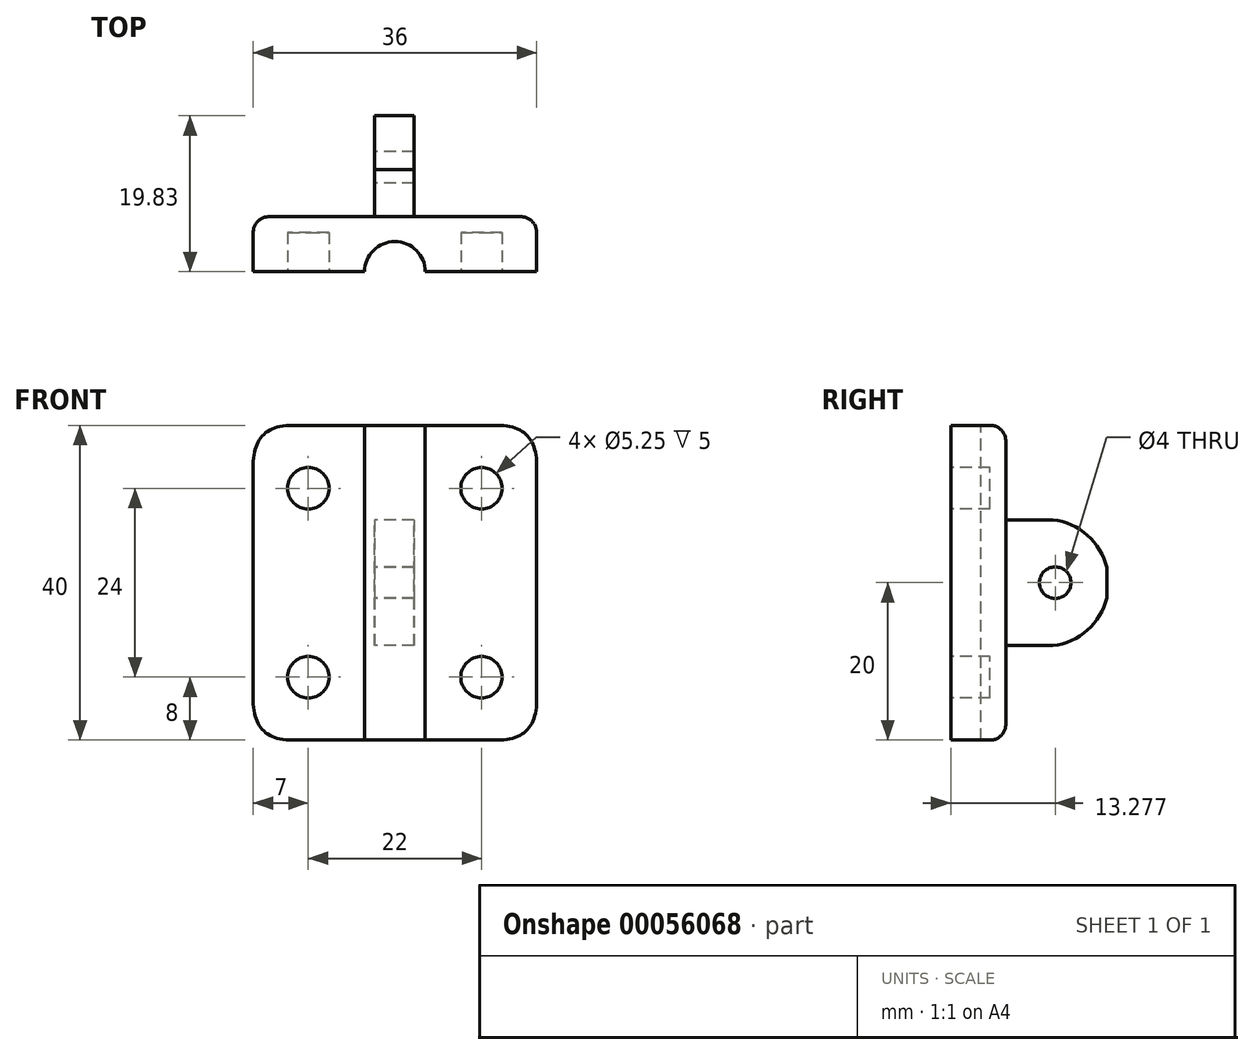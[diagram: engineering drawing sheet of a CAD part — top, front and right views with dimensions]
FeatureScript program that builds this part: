
annotation { "Feature Type Name" : "Feature", "Feature Type Description" : "" }
export const myFeature = defineFeature(function(context is Context, id is Id, definition is map)
    precondition{}
    {
        {
            var Q0;
            Q0=qCreatedBy(makeId("Top.planeOp"),FACE);
            var sketch = newSketch(context, id + "F0", { "sketchPlane" : qUnion([Q0])});
            skLineSegment(sketch, "E0.bottom", {"start": v(-18, 0) * mm, "end": v(18, 0) * mm});
            skLineSegment(sketch, "E0.top", {"start": v(-18, 7) * mm, "end": v(18, 7) * mm});
            skLineSegment(sketch, "E0.left", {"start": v(-18, 0) * mm, "end": v(-18, 7) * mm});
            skLineSegment(sketch, "E0.right", {"start": v(18, 0) * mm, "end": v(18, 7) * mm});
            skSolve(sketch);
        }
        {
            var Q0;
            Q0=makeQuery(id+"F0.imprint","IMPRINT",FACE,{"disambiguationData":[TD([[makeQuery(id+"F0.imprint","IMPRINT",EDGE,{"derivedFrom":sQuery(id+"F0.wireOp",EDGE,"E0.bottom")}),1.0]])]});
            extrude(context, id + "F1", {"entities" : qUnion([Q0]), "depth" : 40 * mm});
        }
        {
            var Q0;
            Q0=makeQuery(id+"F1.opExtrude","CAP_FACE",FACE,{"disambiguationData":[OSD([sQuery(id+"F0.wireOp",EDGE,"E0.bottom"),sQuery(id+"F0.wireOp",EDGE,"E0.top"),sQuery(id+"F0.wireOp",EDGE,"E0.left"),sQuery(id+"F0.wireOp",EDGE,"E0.right")])],"isStart":false});
            var sketch = newSketch(context, id + "F2", { "sketchPlane" : qUnion([Q0])});
            skCircle(sketch, "E1", {"center": v(0, 0) * mm, "radius": 3.85 * mm});
            skSolve(sketch);
        }
        {
            var Q0;
            {var subQ0=sQuery(id+"F2.wireOp",EDGE,"E1");var subQ1=makeQuery(id+"F1.opExtrude","CAP_EDGE",EDGE,{"disambiguationData":[OSD([sQuery(id+"F0.wireOp",EDGE,"E0.bottom")])],"isStart":false});var subQ2=makeQuery(id+"F2.imprint","INTERSECT",VERTEX,{"disambiguationData":[OD(0.0)],"derivedFrom":[subQ1,subQ0]});Q0=makeQuery(id+"F2.imprint","IMPRINT",FACE,{"disambiguationData":[TD([[makeQuery(id+"F2.imprint","IMPRINT",EDGE,{"disambiguationData":[TD([[subQ2,1.0]])],"derivedFrom":subQ0}),1.0]])]});}
            extrude(context, id + "F3", {"entities" : qUnion([Q0]), "operationType" : NewBodyOperationType.REMOVE, "oppositeDirection" : true, "depth" : 50 * mm});
        }
        {
            var Q0;
            {var subQ1=sQuery(id+"F0.wireOp",EDGE,"E0.left");var subQ3=sQuery(id+"F0.wireOp",EDGE,"E0.bottom");Q0=makeQuery(id+"F3.boolean.opBoolean","SPLIT",FACE,{"disambiguationData":[TD([makeQuery(id+"F1.opExtrude","SWEPT_FACE",FACE,{"disambiguationData":[OSD([subQ1])]})])],"derivedFrom":makeQuery(id+"F1.opExtrude","SWEPT_FACE",FACE,{"disambiguationData":[OSD([subQ3])]})});}
            var sketch = newSketch(context, id + "F4", { "sketchPlane" : qUnion([Q0])});
            skCircle(sketch, "E2", {"center": v(-11, 32) * mm, "radius": 2.62 * mm});
            skCircle(sketch, "E3", {"center": v(11, 32) * mm, "radius": 2.62 * mm});
            skCircle(sketch, "E4", {"center": v(11, 8) * mm, "radius": 2.62 * mm});
            skCircle(sketch, "E5", {"center": v(-11, 8) * mm, "radius": 2.62 * mm});
            skSolve(sketch);
        }
        {
            var Q0;
            Q0 = qSketchRegion(id + "F4", true);
            extrude(context, id + "F5", {"entities" : qUnion([Q0]), "operationType" : NewBodyOperationType.REMOVE, "oppositeDirection" : true, "depth" : 5 * mm});
        }
        {
            var Q0;
            Q0=qCreatedBy(makeId("Top.planeOp"),FACE);
            var sketch = newSketch(context, id + "F6", { "sketchPlane" : qUnion([Q0])});
            skLineSegment(sketch, "E6.bottom", {"start": v(-2.58, 4.83) * mm, "end": v(2.42, 4.83) * mm});
            skLineSegment(sketch, "E6.top", {"start": v(-2.58, 19.83) * mm, "end": v(2.42, 19.83) * mm});
            skLineSegment(sketch, "E6.left", {"start": v(-2.58, 4.83) * mm, "end": v(-2.58, 19.83) * mm});
            skLineSegment(sketch, "E6.right", {"start": v(2.42, 4.83) * mm, "end": v(2.42, 19.83) * mm});
            skSolve(sketch);
        }
        {
            var Q0;
            Q0=makeQuery(id+"F6.imprint","IMPRINT",FACE,{"disambiguationData":[TD([[makeQuery(id+"F6.imprint","IMPRINT",EDGE,{"derivedFrom":sQuery(id+"F6.wireOp",EDGE,"E6.bottom")}),1.0]])]});
            extrude(context, id + "F7", {"entities" : qUnion([Q0]), "operationType" : NewBodyOperationType.ADD, "depth" : 40 * mm});
        }
        {
            var Q0;
            Q0=makeQuery(id+"F7.opExtrude","SWEPT_FACE",FACE,{"disambiguationData":[OSD([sQuery(id+"F6.wireOp",EDGE,"E6.left")])]});
            var sketch = newSketch(context, id + "F8", { "sketchPlane" : qUnion([Q0])});
            skLineSegment(sketch, "E7", {"start": v(-7, 12) * mm, "end": v(-13, 12) * mm});
            skLineSegment(sketch, "E8", {"start": v(-7, 28) * mm, "end": v(-13, 28) * mm});
            skLineSegment(sketch, "E9", {"start": v(-7, 28) * mm, "end": v(-7, 40) * mm});
            skLineSegment(sketch, "E10", {"start": v(-7, 12) * mm, "end": v(-7, 0) * mm});
            skArc(sketch, "E11", {"start": v(-13, 28) * mm, "mid": v(-20.06, 20) * mm, "end": v(-13, 12) * mm});
            skLineSegment(sketch, "E12", {"start": v(-7, 0) * mm, "end": v(-19.83, 0) * mm});
            skLineSegment(sketch, "E13", {"start": v(-19.83, 0) * mm, "end": v(-19.83, 40) * mm});
            skLineSegment(sketch, "E14", {"start": v(-19.83, 40) * mm, "end": v(-7, 40) * mm});
            skSolve(sketch);
        }
        {
            var Q0;
            Q0=makeQuery(id+"F8.imprint","IMPRINT",FACE,{"disambiguationData":[TD([[makeQuery(id+"F8.imprint","IMPRINT",EDGE,{"derivedFrom":sQuery(id+"F8.wireOp",EDGE,"E7")}),1.0]])]});
            var Q1;
            {var subQ1=sQuery(id+"F8.wireOp",EDGE,"E8");Q1=makeQuery(id+"F8.imprint","IMPRINT",FACE,{"disambiguationData":[TD([[makeQuery(id+"F8.imprint","IMPRINT",EDGE,{"derivedFrom":subQ1}),-1.0]])]});}
            extrude(context, id + "F9", {"entities" : qUnion([Q0, Q1]), "operationType" : NewBodyOperationType.REMOVE, "oppositeDirection" : true, "depth" : 25 * mm});
        }
        {
            var Q0;
            Q0=makeQuery(id+"F7.opExtrude","SWEPT_FACE",FACE,{"disambiguationData":[OSD([sQuery(id+"F6.wireOp",EDGE,"E6.left")])]});
            var sketch = newSketch(context, id + "F10", { "sketchPlane" : qUnion([Q0])});
            skCircle(sketch, "E15", {"center": v(-13.28, 20) * mm, "radius": 2 * mm});
            skSolve(sketch);
        }
        {
            var Q0;
            Q0=makeQuery(id+"F10.imprint","IMPRINT",FACE,{"disambiguationData":[TD([[makeQuery(id+"F10.imprint","IMPRINT",EDGE,{"derivedFrom":sQuery(id+"F10.wireOp",EDGE,"E15")}),1.0]])]});
            extrude(context, id + "F11", {"entities" : qUnion([Q0]), "operationType" : NewBodyOperationType.REMOVE, "oppositeDirection" : true, "depth" : 25 * mm});
        }
        {
            var Q0;
            Q0=makeQuery(id+"F1.opExtrude","CAP_EDGE",EDGE,{"disambiguationData":[OSD([sQuery(id+"F0.wireOp",EDGE,"E0.right")])],"isStart":true});
            var Q1;
            Q1=makeQuery(id+"F1.opExtrude","CAP_EDGE",EDGE,{"disambiguationData":[OSD([sQuery(id+"F0.wireOp",EDGE,"E0.right")])],"isStart":false});
            var Q2;
            Q2=makeQuery(id+"F1.opExtrude","CAP_EDGE",EDGE,{"disambiguationData":[OSD([sQuery(id+"F0.wireOp",EDGE,"E0.left")])],"isStart":true});
            var Q3;
            Q3=makeQuery(id+"F1.opExtrude","CAP_EDGE",EDGE,{"disambiguationData":[OSD([sQuery(id+"F0.wireOp",EDGE,"E0.left")])],"isStart":false});
            fillet(context, id + "F12", {"entities" : qUnion([Q0, Q1, Q2, Q3]), "radius" : 5 * mm, "tangentPropagation" : true, "rho" : 0.5, "crossSection" : FilletCrossSection.CONIC, "allowEdgeOverflow" : false});
        }
        {
            var Q0;
            Q0=makeQuery(id+"F1.opExtrude","SWEPT_EDGE",EDGE,{"disambiguationData":[OSD([sQuery(id+"F0.wireOp",EDGE,"E0.top"),sQuery(id+"F0.wireOp",EDGE,"E0.left")])]});
            fillet(context, id + "F13", {"entities" : qUnion([Q0]), "radius" : 2 * mm, "tangentPropagation" : true, "allowEdgeOverflow" : false});
        }
    });
